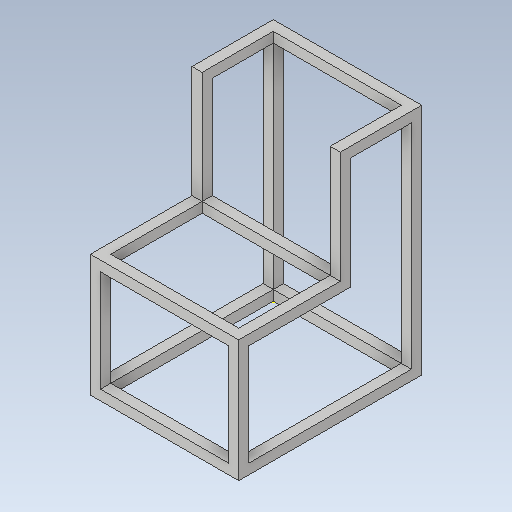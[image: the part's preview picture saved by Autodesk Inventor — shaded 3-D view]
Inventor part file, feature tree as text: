
AUTODESK INVENTOR PART (.ipt)
format: ipt  version: 2020 (Build 240168000, 168)  size: 292,352 bytes
history: native  units: mm
features: sketch x19, extrude x18
ambient origin geometry x8: Origin, YZ Plane, XZ Plane, XY Plane, X Axis, Y Axis, Z Axis, Center Point
bodies: Solid1 (feature_tree)
feature tree (37):
  extrude  "Extrusion1"  Depth=220.0mm
  extrude  "Extrusion2"  Depth=160.0mm
  extrude  "Extrusion3"  Depth=20.0mm
  extrude  "Extrusion4"  Depth=20.0mm
  extrude  "Extrusion5"  Depth=20.0mm
  extrude  "Extrusion6"  Depth=20.0mm
  extrude  "Extrusion7"  Depth=20.0mm
  sketch  "Sketch8"  dims[d18=20.0mm d19=220.0mm d20=0.0mm]
  extrude  "Extrusion8"  Depth=220.0mm TaperAngle=0.0deg
  extrude  "Extrusion9"  Depth=20.0mm
  extrude  "Extrusion10"  Depth=20.0mm
  extrude  "Extrusion11"  Depth=900.0mm TaperAngle=0.0deg
  extrude  "Extrusion12"  Depth=180.0mm TaperAngle=0.0deg
  extrude  "Extrusion13"  Depth=150.0mm TaperAngle=0.0deg
  sketch  "Sketch15"  dims[d40=20.0mm d41=900.0mm d42=0.0mm]
  extrude  "Extrusion14"  Depth=20.0mm TaperAngle=0.0deg
  extrude  "Extrusion15"  Depth=20.0mm TaperAngle=0.0deg
  extrude  "Extrusion16"  Depth=900.0mm TaperAngle=0.0deg
  extrude  "Extrusion17"  Depth=900.0mm TaperAngle=0.0deg
  extrude  "Extrusion18"  Depth=20.0mm
  sketch  "Sketch1"  dims[d0=480.0mm d1=220.0mm]
  sketch  "Sketch2"  dims[d2=360.0mm d3=0.0mm d4=160.0mm]
  sketch  "Sketch3"  dims[d5=20.0mm d6=20.0mm]
  sketch  "Sketch4"  dims[d7=20.0mm d8=20.0mm]
  sketch  "Sketch5"  dims[d9=220.0mm d10=0.0mm d12=20.0mm]
  sketch  "Sketch6"  dims[d13=20.0mm d14=20.0mm]
  sketch  "Sketch7"  dims[d16=20.0mm d17=20.0mm]
  sketch  "Sketch9"  dims[d21=20.0mm d22=20.0mm]
  sketch  "Sketch10"  dims[d23=20.0mm d24=20.0mm]
  sketch  "Sketch11"  dims[d25=600.0mm d26=0.0mm d27=900.0mm d28=0.0mm]
  sketch  "Sketch12"  dims[d29=80.0mm d30=0.0mm d31=180.0mm d32=0.0mm]
  sketch  "Sketch13"  dims[d33=72.0mm d34=0.0mm d35=150.0mm d36=0.0mm]
  sketch  "Sketch14"  dims[d37=20.0mm d38=900.0mm d39=0.0mm]
  sketch  "Sketch16"  dims[d43=900.0mm d44=0.0mm d45=900.0mm d46=0.0mm]
  sketch  "Sketch17"  dims[d47=900.0mm d48=0.0mm d49=900.0mm d50=0.0mm]
  sketch  "Sketch18"  dims[d51=20.0mm d52=0.0mm d53=20.0mm]
  sketch  "Sketch19"  dims[d54=360.0mm d55=0.0mm d56=60.0mm d57=0.0mm]
